# Revit family: 3200 Björk Baby changing station
name_source: partatom
category: Furniture Systems
revit_build: Autodesk Revit 2017 (Build: 20160720_1515(x64)
units: mm (PartAtom-declared; Revit-internal decimal feet)

## family parameters
Always vertical = Yes
Cut with Voids When Loaded = No
Host = Wall
Part Type = Normal
Room Calculation Point = No
Round Connector Dimension = Use Diameter
Shared = No

## types (6) — shared parameters
Down = Yes
Surface = WHITE
Type Image = <None>
UP = No
zero-valued in all types: Cost

## per-type parameters (varying)
| type | Description | Manufacturer | Model | URL |
| BIRK | Touch-free hand dryer | Dan Dryer | Björk-3000 | http://www.dandryer.dk |
| GEO WHITE | Touch-free hand dryer | Dan Dryer | Björk-3000 | http://www.dandryer.dk |
| GRIGIO LONDRA | Touch-free hand dryer | Dan Dryer | Björk-3000 | http://www.dandryer.dk |
| NEGRO INGO | Touch-free hand dryer | Dan Dryer | Björk-3000 | http://www.dandryer.dk |
| OSLO | Baby changing table | Dan Dryer A/S | Björk-3200 | http://www.dandryer.com |
| BIANCO MALE | Touch-free hand dryer | Dan Dryer | Björk-3000 | http://www.dandryer.dk |

## geometry (parser evidence)
native form markers: Sweep x5
no freeform markers — native parametric forms only
